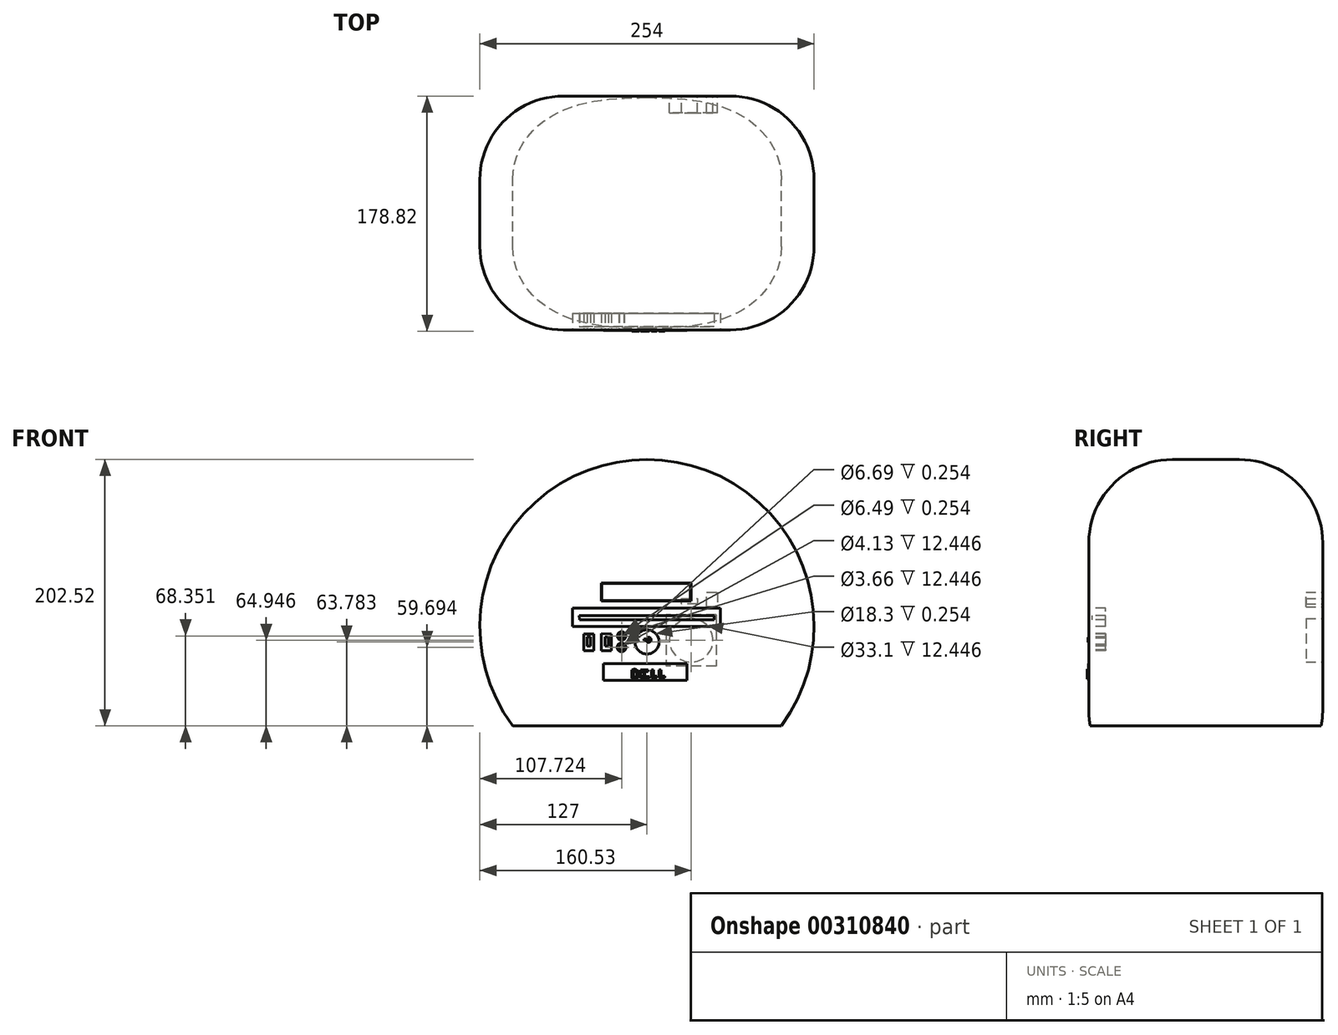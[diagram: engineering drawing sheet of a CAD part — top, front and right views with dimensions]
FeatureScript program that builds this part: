
annotation { "Feature Type Name" : "Feature", "Feature Type Description" : "" }
export const myFeature = defineFeature(function(context is Context, id is Id, definition is map)
    precondition{}
    {
        {
            var Q0;
            Q0=qCreatedBy(makeId("Front.planeOp"),FACE);
            var sketch = newSketch(context, id + "F0", { "sketchPlane" : qUnion([Q0])});
            skCircle(sketch, "E0", {"center": v(0, 0) * mm, "radius": 127 * mm});
            skLineSegment(sketch, "E1", {"start": v(-102.1, -75.52) * mm, "end": v(102.1, -75.52) * mm});
            skSolve(sketch);
        }
        {
            var Q0;
            {var subQ0=sQuery(id+"F0.wireOp",EDGE,"E1");Q0=makeQuery(id+"F0.imprint","IMPRINT",FACE,{"disambiguationData":[TD([[makeQuery(id+"F0.imprint","IMPRINT",EDGE,{"derivedFrom":subQ0}),1.0]])]});}
            extrude(context, id + "F1", {"entities" : qUnion([Q0]), "depth" : 177.8 * mm});
        }
        {
            var Q0;
            Q0=makeQuery(id+"F1.opExtrude","CAP_EDGE",EDGE,{"disambiguationData":[OSD([sQuery(id+"F0.wireOp",EDGE,"E0")])],"isStart":true});
            var Q1;
            Q1=makeQuery(id+"F1.opExtrude","CAP_EDGE",EDGE,{"disambiguationData":[OSD([sQuery(id+"F0.wireOp",EDGE,"E0")])],"isStart":false});
            fillet(context, id + "F2", {"entities" : qUnion([Q0, Q1]), "radius" : 63.5 * mm, "tangentPropagation" : true, "allowEdgeOverflow" : false});
        }
        {
            var Q0;
            Q0=makeQuery(id+"F1.opExtrude","CAP_FACE",FACE,{"disambiguationData":[OSD([sQuery(id+"F0.wireOp",EDGE,"E0"),sQuery(id+"F0.wireOp",EDGE,"E1")])],"isStart":false});
            var sketch = newSketch(context, id + "F3", { "sketchPlane" : qUnion([Q0])});
            skLineSegment(sketch, "E2", {"start": v(-56.6, 0) * mm, "end": v(-56.6, 13.89) * mm});
            skLineSegment(sketch, "E3", {"start": v(-56.6, 13.89) * mm, "end": v(55.84, 13.89) * mm});
            skLineSegment(sketch, "E4", {"start": v(55.84, 13.89) * mm, "end": v(55.84, 0) * mm});
            skLineSegment(sketch, "E5", {"start": v(-56.6, 0) * mm, "end": v(55.84, 0) * mm});
            skLineSegment(sketch, "E6", {"start": v(-51.63, 8.15) * mm, "end": v(50.87, 8.15) * mm});
            skLineSegment(sketch, "E7", {"start": v(50.87, 8.15) * mm, "end": v(50.87, 5.09) * mm});
            skLineSegment(sketch, "E8", {"start": v(50.87, 5.09) * mm, "end": v(-51.25, 5.09) * mm});
            skLineSegment(sketch, "E9", {"start": v(-51.25, 5.09) * mm, "end": v(-51.63, 8.15) * mm});
            skLineSegment(sketch, "E10", {"start": v(-34.8, 19.24) * mm, "end": v(33.66, 19.24) * mm});
            skLineSegment(sketch, "E11", {"start": v(33.66, 19.24) * mm, "end": v(33.66, 33) * mm});
            skLineSegment(sketch, "E12", {"start": v(33.66, 33) * mm, "end": v(-34.8, 33) * mm});
            skLineSegment(sketch, "E13", {"start": v(-34.8, 33) * mm, "end": v(-34.8, 19.24) * mm});
            skLineSegment(sketch, "E14", {"start": v(-48.19, -5.54) * mm, "end": v(-48.19, -18.24) * mm});
            skLineSegment(sketch, "E15", {"start": v(-48.19, -18.24) * mm, "end": v(-40.57, -18.24) * mm});
            skLineSegment(sketch, "E16", {"start": v(-40.57, -18.24) * mm, "end": v(-40.57, -5.54) * mm});
            skLineSegment(sketch, "E17", {"start": v(-40.57, -5.54) * mm, "end": v(-48.19, -5.54) * mm});
            skLineSegment(sketch, "E18", {"start": v(-34.6, -5.5) * mm, "end": v(-34.6, -18.24) * mm});
            skLineSegment(sketch, "E19", {"start": v(-34.6, -18.24) * mm, "end": v(-26.98, -18.24) * mm});
            skLineSegment(sketch, "E20", {"start": v(-26.98, -18.24) * mm, "end": v(-26.98, -5.54) * mm});
            skLineSegment(sketch, "E21", {"start": v(-26.98, -5.54) * mm, "end": v(-34.6, -5.5) * mm});
            skCircle(sketch, "E22", {"center": v(-19.28, -7.17) * mm, "radius": 3.25 * mm});
            skCircle(sketch, "E23", {"center": v(-19.28, -7.17) * mm, "radius": 1.83 * mm});
            skCircle(sketch, "E24", {"center": v(-19.28, -15.83) * mm, "radius": 3.34 * mm});
            skCircle(sketch, "E25", {"center": v(-19.28, -15.83) * mm, "radius": 2.07 * mm});
            skCircle(sketch, "E26", {"center": v(0, -11.74) * mm, "radius": 9.15 * mm});
            skLineSegment(sketch, "E27", {"start": v(-34.24, 32.57) * mm, "end": v(-34.24, 19.84) * mm});
            skLineSegment(sketch, "E28", {"start": v(-34.24, 19.84) * mm, "end": v(32.98, 19.84) * mm});
            skLineSegment(sketch, "E29", {"start": v(32.98, 19.84) * mm, "end": v(32.98, 32.57) * mm});
            skLineSegment(sketch, "E30", {"start": v(32.98, 32.57) * mm, "end": v(-34.24, 32.57) * mm});
            skLineSegment(sketch, "E31", {"start": v(-45.4, -7.87) * mm, "end": v(-42.86, -7.87) * mm});
            skLineSegment(sketch, "E32", {"start": v(-42.86, -7.87) * mm, "end": v(-42.86, -14.9) * mm});
            skLineSegment(sketch, "E33", {"start": v(-42.86, -14.9) * mm, "end": v(-45.4, -14.9) * mm});
            skLineSegment(sketch, "E34", {"start": v(-45.4, -14.9) * mm, "end": v(-45.4, -7.87) * mm});
            skLineSegment(sketch, "E35", {"start": v(-31.7, -7.87) * mm, "end": v(-31.7, -14.9) * mm});
            skLineSegment(sketch, "E36", {"start": v(-31.7, -14.9) * mm, "end": v(-29.16, -14.9) * mm});
            skLineSegment(sketch, "E37", {"start": v(-29.16, -14.9) * mm, "end": v(-29.16, -7.87) * mm});
            skLineSegment(sketch, "E38", {"start": v(-29.16, -7.87) * mm, "end": v(-31.7, -7.87) * mm});
            skLineSegment(sketch, "E39", {"start": v(-33.25, -40.8) * mm, "end": v(-33.25, -28.1) * mm});
            skLineSegment(sketch, "E40", {"start": v(-33.25, -28.1) * mm, "end": v(30.25, -28.1) * mm});
            skLineSegment(sketch, "E41", {"start": v(30.25, -28.1) * mm, "end": v(30.25, -40.8) * mm});
            skLineSegment(sketch, "E42", {"start": v(30.25, -40.8) * mm, "end": v(-33.25, -40.8) * mm});
            skSolve(sketch);
        }
        {
            var Q0;
            Q0=makeQuery(id+"F3.imprint","IMPRINT",FACE,{"disambiguationData":[TD([[makeQuery(id+"F3.imprint","IMPRINT",EDGE,{"derivedFrom":sQuery(id+"F3.wireOp",EDGE,"E18")}),1.0]])]});
            var Q1;
            Q1=makeQuery(id+"F3.imprint","IMPRINT",FACE,{"disambiguationData":[TD([[makeQuery(id+"F3.imprint","IMPRINT",EDGE,{"derivedFrom":sQuery(id+"F3.wireOp",EDGE,"E14")}),1.0]])]});
            var Q2;
            Q2=makeQuery(id+"F3.imprint","IMPRINT",FACE,{"disambiguationData":[TD([[makeQuery(id+"F3.imprint","IMPRINT",EDGE,{"derivedFrom":sQuery(id+"F3.wireOp",EDGE,"E2")}),-1.0]])]});
            var Q3;
            Q3=makeQuery(id+"F3.imprint","IMPRINT",FACE,{"disambiguationData":[TD([[makeQuery(id+"F3.imprint","IMPRINT",EDGE,{"derivedFrom":sQuery(id+"F3.wireOp",EDGE,"E25")}),1.0]])]});
            var Q4;
            Q4=makeQuery(id+"F3.imprint","IMPRINT",FACE,{"disambiguationData":[TD([[makeQuery(id+"F3.imprint","IMPRINT",EDGE,{"derivedFrom":sQuery(id+"F3.wireOp",EDGE,"E23")}),1.0]])]});
            extrude(context, id + "F4", {"entities" : qUnion([Q0, Q1, Q2, Q3, Q4]), "operationType" : NewBodyOperationType.REMOVE, "oppositeDirection" : true, "depth" : 12.7 * mm});
        }
        {
            var Q0;
            Q0=makeQuery(id+"F4.boolean.opBoolean","SPLIT",FACE,{"disambiguationData":[TD([makeQuery(id+"F4.opExtrude","SWEPT_FACE",FACE,{"disambiguationData":[OSD([sQuery(id+"F3.wireOp",EDGE,"E6")])]})])],"derivedFrom":makeQuery(id+"F1.opExtrude","CAP_FACE",FACE,{"disambiguationData":[OSD([sQuery(id+"F0.wireOp",EDGE,"E0"),sQuery(id+"F0.wireOp",EDGE,"E1")])],"isStart":false})});
            extrude(context, id + "F5", {"entities" : qUnion([Q0]), "operationType" : NewBodyOperationType.REMOVE, "oppositeDirection" : true, "depth" : 2.54 * mm});
        }
        {
            var Q0;
            Q0=makeQuery(id+"F3.imprint","IMPRINT",FACE,{"disambiguationData":[TD([[makeQuery(id+"F3.imprint","IMPRINT",EDGE,{"derivedFrom":sQuery(id+"F3.wireOp",EDGE,"E10")}),1.0]])]});
            extrude(context, id + "F6", {"entities" : qUnion([Q0]), "operationType" : NewBodyOperationType.REMOVE, "oppositeDirection" : true, "depth" : 0.03 * mm});
        }
        {
            var Q0;
            Q0=makeQuery(id+"F3.imprint","IMPRINT",FACE,{"disambiguationData":[TD([[makeQuery(id+"F3.imprint","IMPRINT",EDGE,{"derivedFrom":sQuery(id+"F3.wireOp",EDGE,"E22")}),1.0]])]});
            var Q1;
            Q1=makeQuery(id+"F3.imprint","IMPRINT",FACE,{"disambiguationData":[TD([[makeQuery(id+"F3.imprint","IMPRINT",EDGE,{"derivedFrom":sQuery(id+"F3.wireOp",EDGE,"E24")}),1.0]])]});
            extrude(context, id + "F7", {"entities" : qUnion([Q0, Q1]), "operationType" : NewBodyOperationType.REMOVE, "oppositeDirection" : true, "depth" : 0.25 * mm});
        }
        {
            var Q0;
            Q0=makeQuery(id+"F3.imprint","IMPRINT",FACE,{"disambiguationData":[TD([[makeQuery(id+"F3.imprint","IMPRINT",EDGE,{"derivedFrom":sQuery(id+"F3.wireOp",EDGE,"E26")}),1.0]])]});
            extrude(context, id + "F8", {"entities" : qUnion([Q0]), "operationType" : NewBodyOperationType.REMOVE, "oppositeDirection" : true, "depth" : 0.25 * mm});
        }
        {
            var Q0;
            Q0=makeQuery(id+"F8.boolean.opBoolean","COPY",FACE,{"derivedFrom":makeQuery(id+"F8.opExtrude","CAP_FACE",FACE,{"disambiguationData":[OSD([sQuery(id+"F3.wireOp",EDGE,"E26")])],"isStart":false})});
            var sketch = newSketch(context, id + "F9", { "sketchPlane" : qUnion([Q0])});
            skArc(sketch, "E43", {"start": v(0, -11.74) * mm, "mid": v(3.13, -10.11) * mm, "end": v(0, -8.5) * mm});
            skArc(sketch, "E44", {"start": v(0, -11.74) * mm, "mid": v(2.39, -10.11) * mm, "end": v(0, -8.5) * mm});
            skLineSegment(sketch, "E45", {"start": v(0.64, -9.53) * mm, "end": v(-2.2, -9.53) * mm});
            skLineSegment(sketch, "E46", {"start": v(-2.2, -9.53) * mm, "end": v(-2.2, -10.7) * mm});
            skLineSegment(sketch, "E47", {"start": v(-2.2, -10.7) * mm, "end": v(0.64, -10.7) * mm});
            skLineSegment(sketch, "E48", {"start": v(0.64, -10.7) * mm, "end": v(0.64, -9.53) * mm});
            skSolve(sketch);
        }
        {
            var Q0;
            Q0=makeQuery(id+"F9.imprint","IMPRINT",FACE,{"disambiguationData":[TD([[makeQuery(id+"F9.imprint","IMPRINT",EDGE,{"derivedFrom":sQuery(id+"F9.wireOp",EDGE,"E45")}),1.0]])]});
            var Q1;
            Q1=makeQuery(id+"F9.imprint","IMPRINT",FACE,{"disambiguationData":[TD([[makeQuery(id+"F9.imprint","IMPRINT",EDGE,{"derivedFrom":sQuery(id+"F9.wireOp",EDGE,"E43")}),1.0]])]});
            extrude(context, id + "F10", {"entities" : qUnion([Q0, Q1]), "operationType" : NewBodyOperationType.ADD, "depth" : 0.76 * mm});
        }
        {
            var Q0;
            Q0=makeQuery(id+"F1.opExtrude","CAP_FACE",FACE,{"disambiguationData":[OSD([sQuery(id+"F0.wireOp",EDGE,"E0"),sQuery(id+"F0.wireOp",EDGE,"E1")])],"isStart":true});
            var sketch = newSketch(context, id + "F11", { "sketchPlane" : qUnion([Q0])});
            skLineSegment(sketch, "E49", {"start": v(-52.58, 9.05) * mm, "end": v(-14.48, 9.05) * mm});
            skLineSegment(sketch, "E50", {"start": v(-14.48, 9.05) * mm, "end": v(-14.48, -30.2) * mm});
            skLineSegment(sketch, "E51", {"start": v(-52.58, 9.05) * mm, "end": v(-52.58, -30.2) * mm});
            skLineSegment(sketch, "E52", {"start": v(-52.58, -30.2) * mm, "end": v(-14.48, -30.2) * mm});
            skCircle(sketch, "E53", {"center": v(-33.53, -10.57) * mm, "radius": 16.55 * mm});
            skPoint(sketch, "E53.centerSnap0", {"position": v(-14.48, -10.57) * mm});
            skPoint(sketch, "E53.centerSnap1", {"position": v(-33.53, -30.2) * mm});
            skLineSegment(sketch, "E54", {"start": v(-23.7, 14.97) * mm, "end": v(-23.7, 21.18) * mm});
            skLineSegment(sketch, "E55", {"start": v(-23.7, 21.18) * mm, "end": v(-27.33, 24.97) * mm});
            skLineSegment(sketch, "E56", {"start": v(-27.33, 24.97) * mm, "end": v(-36.75, 24.97) * mm});
            skLineSegment(sketch, "E57", {"start": v(-36.75, 24.97) * mm, "end": v(-40.73, 21.18) * mm});
            skLineSegment(sketch, "E58", {"start": v(-41.04, 14.97) * mm, "end": v(-40.73, 21.18) * mm});
            skLineSegment(sketch, "E59", {"start": v(-41.04, 14.97) * mm, "end": v(-23.7, 14.97) * mm});
            skLineSegment(sketch, "E60", {"start": v(-38.22, 17.11) * mm, "end": v(-26.26, 17.11) * mm});
            skLineSegment(sketch, "E61", {"start": v(-26.26, 17.11) * mm, "end": v(-26.26, 21.23) * mm});
            skLineSegment(sketch, "E62", {"start": v(-26.26, 21.23) * mm, "end": v(-38.22, 21.23) * mm});
            skLineSegment(sketch, "E63", {"start": v(-38.22, 21.23) * mm, "end": v(-38.22, 17.11) * mm});
            skLineSegment(sketch, "E64", {"start": v(-45.3, 14.97) * mm, "end": v(-45.3, 26) * mm});
            skLineSegment(sketch, "E65", {"start": v(-45.3, 26) * mm, "end": v(-53.45, 26) * mm});
            skLineSegment(sketch, "E66", {"start": v(-53.45, 26) * mm, "end": v(-53.45, 14.97) * mm});
            skLineSegment(sketch, "E67", {"start": v(-53.45, 14.97) * mm, "end": v(-45.3, 14.97) * mm});
            skSolve(sketch);
        }
        {
            var Q0;
            Q0=makeQuery(id+"F11.imprint","IMPRINT",FACE,{"disambiguationData":[TD([[makeQuery(id+"F11.imprint","IMPRINT",EDGE,{"derivedFrom":sQuery(id+"F11.wireOp",EDGE,"E53")}),1.0]])]});
            var Q1;
            Q1=makeQuery(id+"F11.imprint","IMPRINT",FACE,{"disambiguationData":[TD([[makeQuery(id+"F11.imprint","IMPRINT",EDGE,{"derivedFrom":sQuery(id+"F11.wireOp",EDGE,"E60")}),1.0]])]});
            var Q2;
            Q2=makeQuery(id+"F11.imprint","IMPRINT",FACE,{"disambiguationData":[TD([[makeQuery(id+"F11.imprint","IMPRINT",EDGE,{"derivedFrom":sQuery(id+"F11.wireOp",EDGE,"E64")}),1.0]])]});
            extrude(context, id + "F12", {"entities" : qUnion([Q0, Q1, Q2]), "operationType" : NewBodyOperationType.REMOVE, "oppositeDirection" : true, "depth" : 12.7 * mm});
        }
        {
            var Q0;
            Q0=makeQuery(id+"F11.imprint","IMPRINT",FACE,{"disambiguationData":[TD([[makeQuery(id+"F11.imprint","IMPRINT",EDGE,{"derivedFrom":sQuery(id+"F11.wireOp",EDGE,"E49")}),-1.0]])]});
            extrude(context, id + "F13", {"entities" : qUnion([Q0]), "operationType" : NewBodyOperationType.REMOVE, "oppositeDirection" : true, "depth" : 0.25 * mm});
        }
        {
            var Q0;
            Q0=makeQuery(id+"F3.imprint","IMPRINT",FACE,{"disambiguationData":[TD([[makeQuery(id+"F3.imprint","IMPRINT",EDGE,{"derivedFrom":sQuery(id+"F3.wireOp",EDGE,"E39")}),-1.0]])]});
            extrude(context, id + "F14", {"entities" : qUnion([Q0]), "operationType" : NewBodyOperationType.ADD, "depth" : 0.25 * mm});
        }
        {
            var Q0;
            Q0=makeQuery(id+"F14.opExtrude","CAP_FACE",FACE,{"disambiguationData":[OSD([sQuery(id+"F3.wireOp",EDGE,"E39"),sQuery(id+"F3.wireOp",EDGE,"E40"),sQuery(id+"F3.wireOp",EDGE,"E41"),sQuery(id+"F3.wireOp",EDGE,"E42")])],"isStart":false});
            var sketch = newSketch(context, id + "F15", { "sketchPlane" : qUnion([Q0])});
            skLineSegment(sketch, "E68", {"start": v(-4.7, -33.02) * mm, "end": v(0.85, -33.02) * mm});
            skLineSegment(sketch, "E69", {"start": v(0.85, -33.02) * mm, "end": v(0.85, -34.14) * mm});
            skLineSegment(sketch, "E70", {"start": v(0.85, -34.14) * mm, "end": v(-3.24, -34.14) * mm});
            skLineSegment(sketch, "E71", {"start": v(-3.24, -34.14) * mm, "end": v(-3.24, -35.62) * mm});
            skLineSegment(sketch, "E72", {"start": v(-3.24, -35.62) * mm, "end": v(-1.57, -35.62) * mm});
            skLineSegment(sketch, "E73", {"start": v(-1.57, -35.62) * mm, "end": v(-1.57, -36.7) * mm});
            skLineSegment(sketch, "E74", {"start": v(-1.57, -36.7) * mm, "end": v(-3.24, -36.7) * mm});
            skLineSegment(sketch, "E75", {"start": v(-3.24, -36.7) * mm, "end": v(-3.24, -38.19) * mm});
            skLineSegment(sketch, "E76", {"start": v(-3.24, -38.19) * mm, "end": v(1.93, -38.19) * mm});
            skLineSegment(sketch, "E77", {"start": v(1.93, -38.19) * mm, "end": v(1.93, -39.37) * mm});
            skLineSegment(sketch, "E78", {"start": v(1.93, -39.37) * mm, "end": v(-4.75, -39.37) * mm});
            skLineSegment(sketch, "E79", {"start": v(-4.75, -39.37) * mm, "end": v(-4.7, -33.02) * mm});
            skLineSegment(sketch, "E80", {"start": v(-11.62, -33.02) * mm, "end": v(-11.62, -39.37) * mm});
            skArc(sketch, "E81", {"start": v(-11.62, -39.37) * mm, "mid": v(-5.95, -36.2) * mm, "end": v(-11.62, -33.02) * mm});
            skLineSegment(sketch, "E82", {"start": v(3.32, -33.02) * mm, "end": v(3.32, -39.03) * mm});
            skLineSegment(sketch, "E83", {"start": v(3.32, -39.03) * mm, "end": v(7.65, -39.03) * mm});
            skLineSegment(sketch, "E84", {"start": v(7.65, -39.03) * mm, "end": v(7.65, -37.72) * mm});
            skLineSegment(sketch, "E85", {"start": v(7.65, -37.72) * mm, "end": v(4.86, -37.72) * mm});
            skLineSegment(sketch, "E86", {"start": v(4.86, -37.72) * mm, "end": v(4.86, -33.02) * mm});
            skLineSegment(sketch, "E87", {"start": v(4.86, -33.02) * mm, "end": v(3.32, -33.02) * mm});
            skLineSegment(sketch, "E88", {"start": v(9.11, -33.02) * mm, "end": v(9.11, -39.03) * mm});
            skLineSegment(sketch, "E89", {"start": v(9.11, -39.03) * mm, "end": v(13.53, -39.03) * mm});
            skLineSegment(sketch, "E90", {"start": v(13.53, -39.03) * mm, "end": v(13.53, -37.66) * mm});
            skLineSegment(sketch, "E91", {"start": v(13.53, -37.66) * mm, "end": v(10.67, -37.66) * mm});
            skLineSegment(sketch, "E92", {"start": v(10.67, -37.66) * mm, "end": v(10.67, -33.02) * mm});
            skLineSegment(sketch, "E93", {"start": v(9.11, -33.02) * mm, "end": v(10.67, -33.02) * mm});
            skLineSegment(sketch, "E94", {"start": v(-10.34, -33.85) * mm, "end": v(-10.34, -38.84) * mm});
            skArc(sketch, "E95", {"start": v(-10.34, -38.84) * mm, "mid": v(-7.68, -36.35) * mm, "end": v(-10.34, -33.85) * mm});
            skSolve(sketch);
        }
        {
            var Q0;
            Q0=makeQuery(id+"F15.imprint","IMPRINT",FACE,{"disambiguationData":[TD([[makeQuery(id+"F15.imprint","IMPRINT",EDGE,{"derivedFrom":sQuery(id+"F15.wireOp",EDGE,"E80")}),1.0]])]});
            var Q1;
            Q1=makeQuery(id+"F15.imprint","IMPRINT",FACE,{"disambiguationData":[TD([[makeQuery(id+"F15.imprint","IMPRINT",EDGE,{"derivedFrom":sQuery(id+"F15.wireOp",EDGE,"E68")}),-1.0]])]});
            var Q2;
            Q2=makeQuery(id+"F15.imprint","IMPRINT",FACE,{"disambiguationData":[TD([[makeQuery(id+"F15.imprint","IMPRINT",EDGE,{"derivedFrom":sQuery(id+"F15.wireOp",EDGE,"E82")}),1.0]])]});
            var Q3;
            Q3=makeQuery(id+"F15.imprint","IMPRINT",FACE,{"disambiguationData":[TD([[makeQuery(id+"F15.imprint","IMPRINT",EDGE,{"derivedFrom":sQuery(id+"F15.wireOp",EDGE,"E88")}),1.0]])]});
            extrude(context, id + "F16", {"entities" : qUnion([Q0, Q1, Q2, Q3]), "operationType" : NewBodyOperationType.ADD, "depth" : 0.76 * mm});
        }
    });
